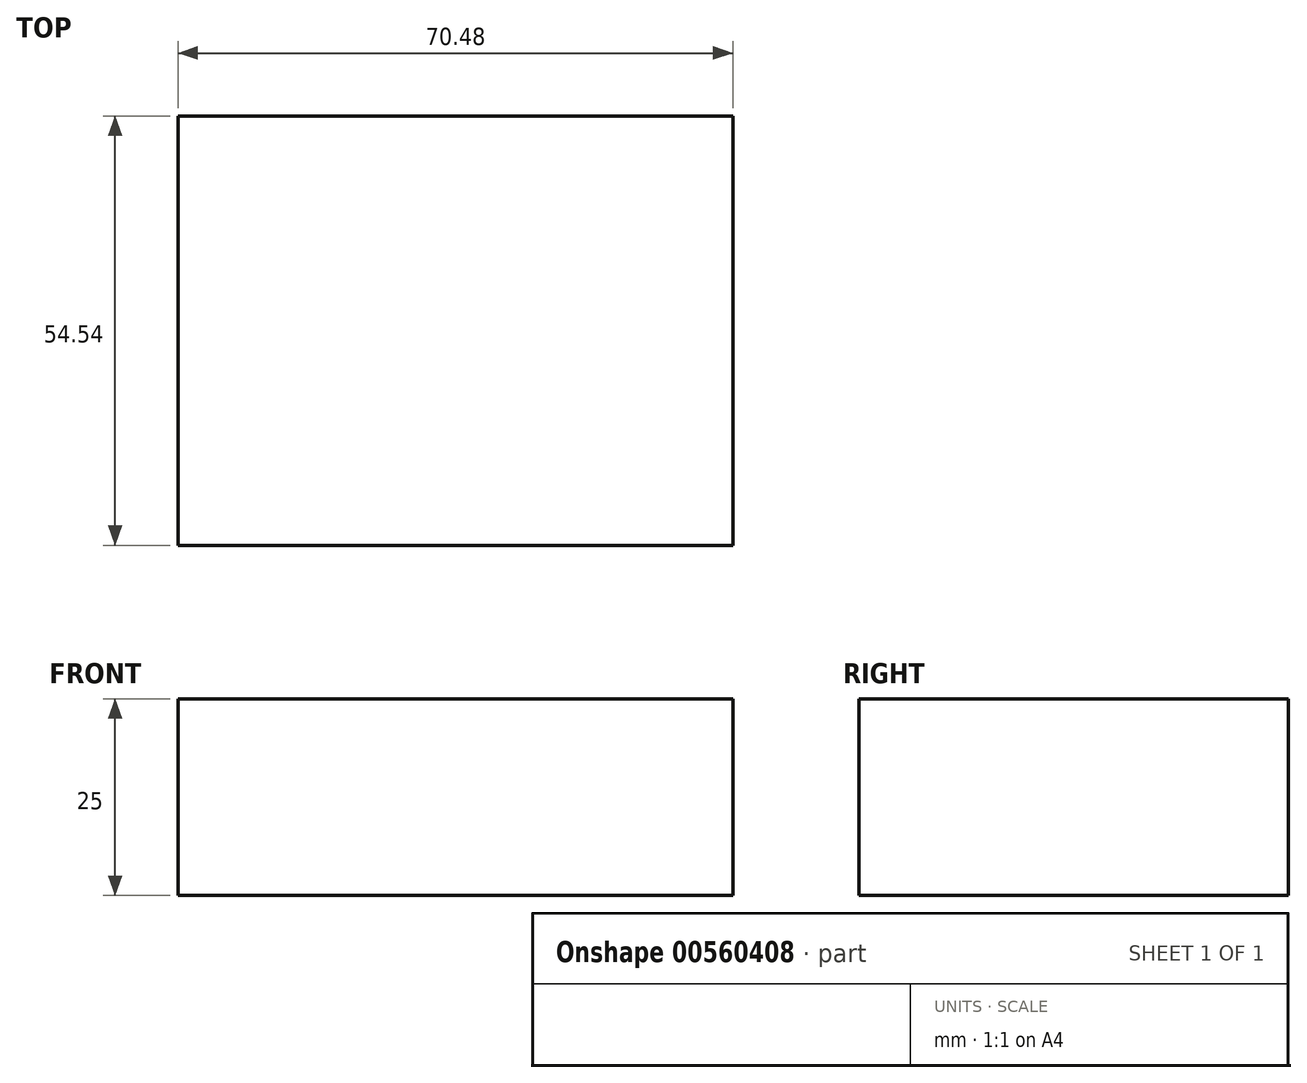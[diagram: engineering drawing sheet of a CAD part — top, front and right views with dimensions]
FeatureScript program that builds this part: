
annotation { "Feature Type Name" : "Feature", "Feature Type Description" : "" }
export const myFeature = defineFeature(function(context is Context, id is Id, definition is map)
    precondition{}
    {
        {
            var Q0;
            Q0=qCreatedBy(makeId("Top.planeOp"),FACE);
            var sketch = newSketch(context, id + "F0", { "sketchPlane" : qUnion([Q0])});
            skLineSegment(sketch, "E0.bottom", {"start": v(-36.42, 27.96) * mm, "end": v(34.06, 27.96) * mm});
            skLineSegment(sketch, "E0.top", {"start": v(-36.42, -26.58) * mm, "end": v(34.06, -26.58) * mm});
            skLineSegment(sketch, "E0.left", {"start": v(-36.42, 27.96) * mm, "end": v(-36.42, -26.58) * mm});
            skLineSegment(sketch, "E0.right", {"start": v(34.06, 27.96) * mm, "end": v(34.06, -26.58) * mm});
            skSolve(sketch);
        }
        {
            var Q0;
            Q0=makeQuery(id+"F0.imprint","IMPRINT",FACE,{"disambiguationData":[TD([[makeQuery(id+"F0.imprint","IMPRINT",EDGE,{"derivedFrom":sQuery(id+"F0.wireOp",EDGE,"E0.bottom")}),-1.0]])]});
            extrude(context, id + "F1", {"entities" : qUnion([Q0]), "depth" : 25 * mm, "offsetDistance" : 25 * mm});
        }
    });
